# Revit family: FU_Table_Sandler_591AT-MT
name_source: partatom
category: Furniture
units: mm (PartAtom-declared; Revit-internal decimal feet)

## family parameters
Always vertical = Yes
Cut with Voids When Loaded = No
OmniClass Number = 23.40.20.00
OmniClass Title = General Furniture and Specialties
Room Calculation Point = No
Shared = No
Work Plane-Based = No

## types (4) — shared parameters
Depth = 397 mm  [stored 1.30249 ft]
Description = Double column table base. Available in powdercoat and painted finishes.
Optional upcharge for outdoor version with galvanized-treated frame and adjustable feet.
Height = 1100 mm  [stored 3.60892 ft]
Manufacturer = Sandler
Model = 591AT-MT
Top Elevation = 1100 mm  [stored 3.60892 ft]
URL = https://www.sandlerseating.com
Width = 747 mm  [stored 2.45079 ft]
zero-valued in all types: Default Elevation

## per-type parameters (varying)
| type | Top Type |
| 591AT-MT - 28x48" Top | FU_TableTops_591 MT : 28x48" Top (70x120cm) |
| 591AT-MT - 28x52" Top | FU_TableTops_591 MT : 28x52" Top (70x130cm) |
| 591AT-MT - 32x48" Top | FU_TableTops_591 MT : 32x48" Top (80x120cm) |
| 591AT-MT - 32x52" Top | FU_TableTops_591 MT : 32x52" Top (80x130cm) |

note: [stored X ft] marks values corroborated as IEEE doubles in the binary element streams (Revit-internal decimal feet)

## geometry (parser evidence)
native form markers: Sweep x3
no freeform markers — native parametric forms only
